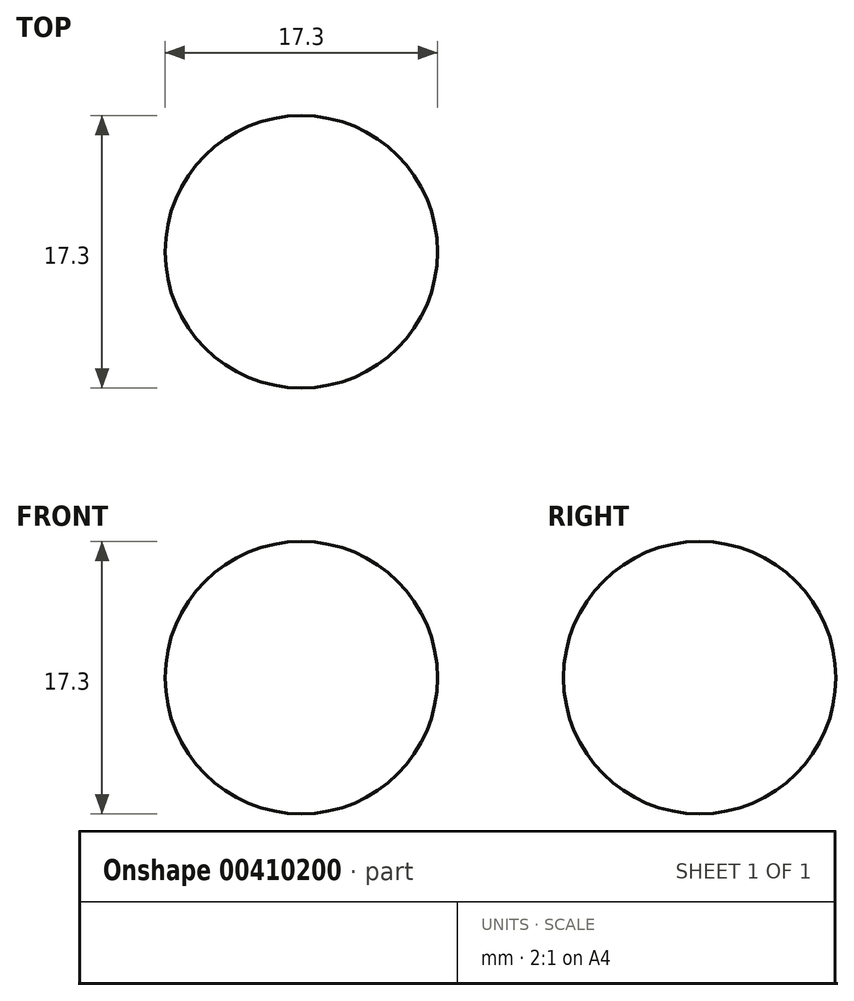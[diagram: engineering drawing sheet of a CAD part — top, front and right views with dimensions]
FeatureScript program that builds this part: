
annotation { "Feature Type Name" : "Feature", "Feature Type Description" : "" }
export const myFeature = defineFeature(function(context is Context, id is Id, definition is map)
    precondition{}
    {
        {
            var Q0;
            Q0=qCreatedBy(makeId("Front.planeOp"),FACE);
            var sketch = newSketch(context, id + "F0", { "sketchPlane" : qUnion([Q0])});
            skArc(sketch, "E0", {"start": v(0, 8.65) * mm, "mid": v(-8.65, 0) * mm, "end": v(0, -8.65) * mm});
            skLineSegment(sketch, "E1", {"start": v(0, -8.65) * mm, "end": v(0, 8.65) * mm});
            skSolve(sketch);
        }
        {
            var Q0;
            Q0 = qSketchRegion(id + "F0", true);
            var Q1;
            Q1=sQuery(id+"F0.wireOp",EDGE,"E1");
            revolve(context, id + "F1", {"entities" : qUnion([Q0]), "axis" : qUnion([Q1]), "revolveType" : RevolveType.FULL});
        }
    });
